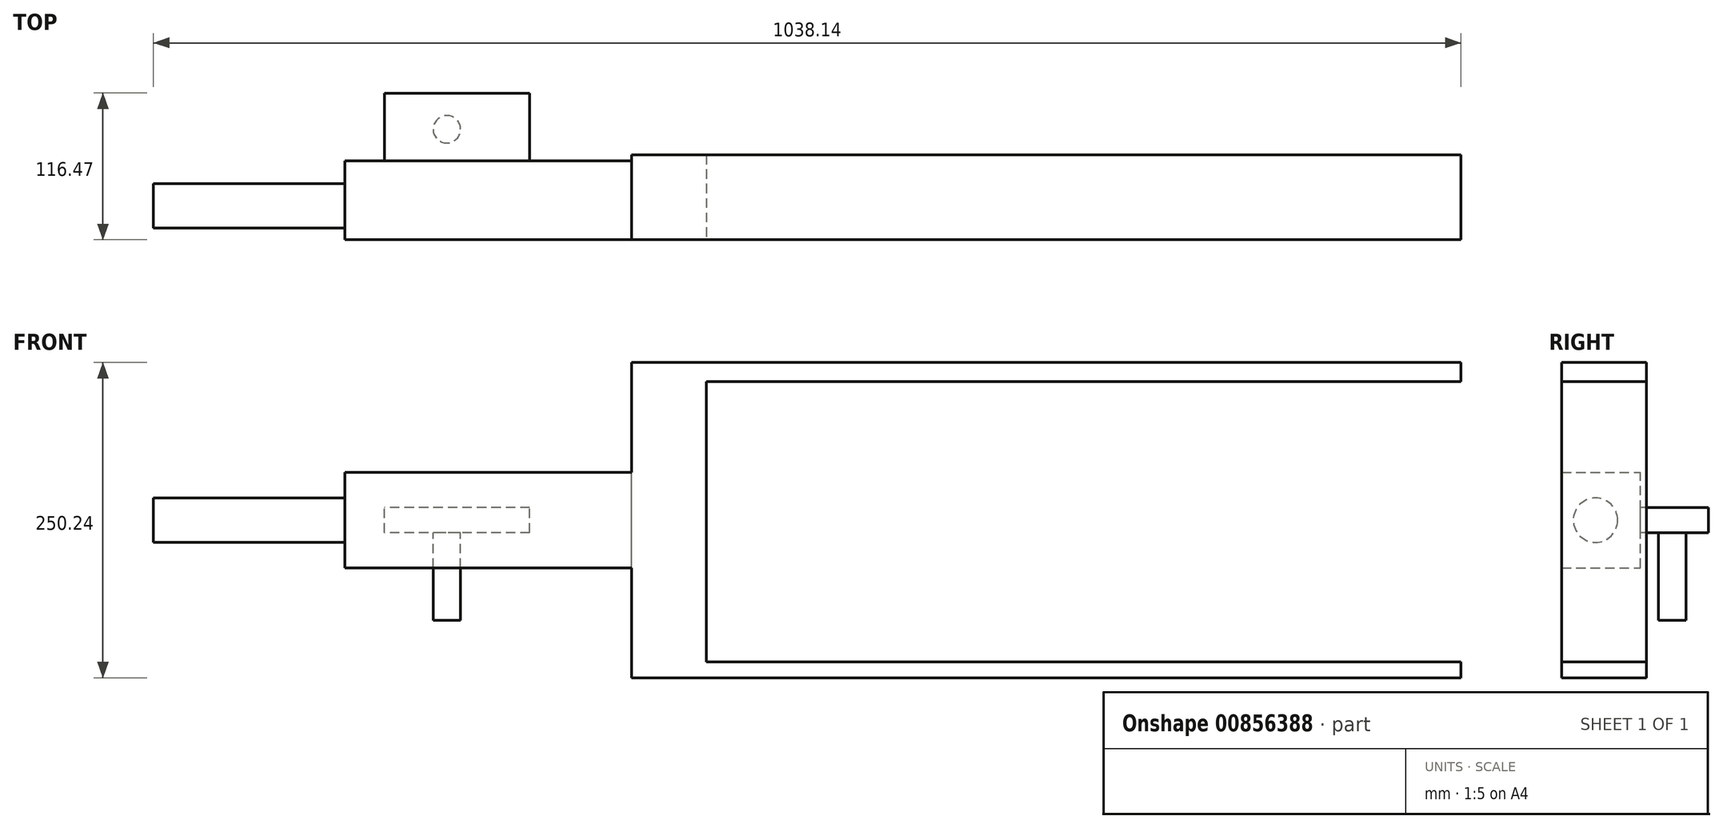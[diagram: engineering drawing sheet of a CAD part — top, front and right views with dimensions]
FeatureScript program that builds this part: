
annotation { "Feature Type Name" : "Feature", "Feature Type Description" : "" }
export const myFeature = defineFeature(function(context is Context, id is Id, definition is map)
    precondition{}
    {
        {
            var Q0;
            Q0=qCreatedBy(makeId("Front.planeOp"),FACE);
            var sketch = newSketch(context, id + "F0", { "sketchPlane" : qUnion([Q0])});
            skLineSegment(sketch, "E0.bottom", {"start": v(-29.7, -125.12) * mm, "end": v(29.7, -125.12) * mm});
            skLineSegment(sketch, "E0.top", {"start": v(-29.7, 125.12) * mm, "end": v(29.7, 125.12) * mm});
            skLineSegment(sketch, "E0.left", {"start": v(-29.7, -125.12) * mm, "end": v(-29.7, 125.12) * mm});
            skLineSegment(sketch, "E0.right", {"start": v(29.7, -125.12) * mm, "end": v(29.7, 125.12) * mm});
            skPoint(sketch, "E0.middle", {"position": v(0, 0) * mm});
            skSolve(sketch);
        }
        {
            var Q0;
            Q0 = qSketchRegion(id + "FCx6LNqj2EdK9tp_0", true);
            var Q1;
            Q1=makeQuery(id+"F0.imprint","IMPRINT",FACE,{"disambiguationData":[TD([[makeQuery(id+"F0.imprint","IMPRINT",EDGE,{"derivedFrom":sQuery(id+"F0.wireOp",EDGE,"E0.bottom")}),1.0]])]});
            extrude(context, id + "F1", {"entities" : qUnion([Q0, Q1]), "depth" : 67.44 * mm, "offsetDistance" : 25.4 * mm});
        }
        {
            var Q0;
            Q0=makeQuery(id+"F1.opExtrude","SWEPT_FACE",FACE,{"disambiguationData":[OSD([sQuery(id+"F0.wireOp",EDGE,"E0.top")])]});
            var sketch = newSketch(context, id + "F2", { "sketchPlane" : qUnion([Q0])});
            skCircle(sketch, "E1", {"center": v(0, -33.22) * mm, "radius": 17.43 * mm});
            skPoint(sketch, "E1.centerSnap0", {"position": v(0, -67.44) * mm});
            skSolve(sketch);
        }
        {
            var Q0;
            Q0=makeQuery(id+"F2.imprint","IMPRINT",FACE,{"disambiguationData":[TD([[makeQuery(id+"F2.imprint","IMPRINT",EDGE,{"derivedFrom":sQuery(id+"F2.wireOp",EDGE,"E1")}),1.0]])]});
            extrude(context, id + "F3", {"entities" : qUnion([Q0]), "operationType" : NewBodyOperationType.ADD, "oppositeDirection" : true, "depth" : 222.84 * mm, "offsetDistance" : 25.4 * mm});
        }
        {
            var Q0;
            Q0=makeQuery(id+"F1.opExtrude","SWEPT_FACE",FACE,{"disambiguationData":[OSD([sQuery(id+"F0.wireOp",EDGE,"E0.left")])]});
            var sketch = newSketch(context, id + "F4", { "sketchPlane" : qUnion([Q0])});
            skLineSegment(sketch, "E2.bottom", {"start": v(67.44, -37.79) * mm, "end": v(4.93, -37.79) * mm});
            skLineSegment(sketch, "E2.top", {"start": v(67.44, 37.79) * mm, "end": v(4.93, 37.79) * mm});
            skLineSegment(sketch, "E2.left", {"start": v(67.44, -37.79) * mm, "end": v(67.44, 37.79) * mm});
            skLineSegment(sketch, "E2.right", {"start": v(4.93, -37.79) * mm, "end": v(4.93, 37.79) * mm});
            skPoint(sketch, "E2.middle", {"position": v(36.18, 0) * mm});
            skSolve(sketch);
        }
        {
            var Q0;
            Q0=makeQuery(id+"F4.imprint","IMPRINT",FACE,{"disambiguationData":[TD([[makeQuery(id+"F4.imprint","IMPRINT",EDGE,{"derivedFrom":sQuery(id+"F4.wireOp",EDGE,"E2.bottom")}),-1.0]])]});
            extrude(context, id + "F5", {"entities" : qUnion([Q0]), "operationType" : NewBodyOperationType.ADD, "depth" : 227.65 * mm, "offsetDistance" : 25.4 * mm});
        }
        {
            var Q0;
            Q0=makeQuery(id+"F5.opExtrude","SWEPT_FACE",FACE,{"disambiguationData":[OSD([sQuery(id+"F4.wireOp",EDGE,"E2.right")])]});
            var sketch = newSketch(context, id + "F6", { "sketchPlane" : qUnion([Q0])});
            skLineSegment(sketch, "E3.bottom", {"start": v(110.41, -9.9) * mm, "end": v(225.7, -9.9) * mm});
            skLineSegment(sketch, "E3.top", {"start": v(110.41, 9.9) * mm, "end": v(225.7, 9.9) * mm});
            skLineSegment(sketch, "E3.left", {"start": v(110.41, -9.9) * mm, "end": v(110.41, 9.9) * mm});
            skLineSegment(sketch, "E3.right", {"start": v(225.7, -9.9) * mm, "end": v(225.7, 9.9) * mm});
            skPoint(sketch, "E3.middle", {"position": v(168.05, 0) * mm});
            skSolve(sketch);
        }
        {
            var Q0;
            Q0 = qSketchRegion(id + "F6", true);
            extrude(context, id + "F7", {"entities" : qUnion([Q0]), "operationType" : NewBodyOperationType.ADD, "depth" : 53.96 * mm, "offsetDistance" : 25.4 * mm});
        }
        {
            var Q0;
            Q0=makeQuery(id+"F1.opExtrude","SWEPT_FACE",FACE,{"disambiguationData":[OSD([sQuery(id+"F0.wireOp",EDGE,"E0.right")])]});
            var sketch = newSketch(context, id + "F8", { "sketchPlane" : qUnion([Q0])});
            skLineSegment(sketch, "E4.bottom", {"start": v(0, -125.12) * mm, "end": v(-67.44, -125.12) * mm});
            skLineSegment(sketch, "E4.top", {"start": v(0, -112.46) * mm, "end": v(-67.44, -112.46) * mm});
            skLineSegment(sketch, "E4.left", {"start": v(0, -125.12) * mm, "end": v(0, -112.46) * mm});
            skLineSegment(sketch, "E4.right", {"start": v(-67.44, -125.12) * mm, "end": v(-67.44, -112.46) * mm});
            skLineSegment(sketch, "E5.bottom", {"start": v(0, 125.12) * mm, "end": v(-67.44, 125.12) * mm});
            skLineSegment(sketch, "E5.top", {"start": v(0, 110.1) * mm, "end": v(-67.44, 110.1) * mm});
            skLineSegment(sketch, "E5.left", {"start": v(0, 125.12) * mm, "end": v(0, 110.1) * mm});
            skLineSegment(sketch, "E5.right", {"start": v(-67.44, 125.12) * mm, "end": v(-67.44, 110.1) * mm});
            skSolve(sketch);
        }
        {
            var Q0;
            Q0 = qSketchRegion(id + "F8", true);
            extrude(context, id + "F9", {"entities" : qUnion([Q0]), "operationType" : NewBodyOperationType.ADD, "depth" : 599.2 * mm, "offsetDistance" : 25.4 * mm});
        }
        {
            var Q0;
            Q0=makeQuery(id+"F5.opExtrude","CAP_FACE",FACE,{"disambiguationData":[OSD([sQuery(id+"F4.wireOp",EDGE,"E2.bottom"),sQuery(id+"F4.wireOp",EDGE,"E2.top"),sQuery(id+"F4.wireOp",EDGE,"E2.left"),sQuery(id+"F4.wireOp",EDGE,"E2.right")])],"isStart":false});
            var sketch = newSketch(context, id + "F10", { "sketchPlane" : qUnion([Q0])});
            skCircle(sketch, "E6", {"center": v(40.56, 0) * mm, "radius": 17.59 * mm});
            skSolve(sketch);
        }
        {
            var Q0;
            Q0=makeQuery(id+"F10.imprint","IMPRINT",FACE,{"disambiguationData":[TD([[makeQuery(id+"F10.imprint","IMPRINT",EDGE,{"derivedFrom":sQuery(id+"F10.wireOp",EDGE,"E6")}),1.0]])]});
            var Q1;
            Q1 = qSketchRegion(id + "F10", true);
            extrude(context, id + "F11", {"entities" : qUnion([Q0, Q1]), "operationType" : NewBodyOperationType.ADD, "depth" : 151.89 * mm, "offsetDistance" : 25.4 * mm});
        }
        {
            var Q0;
            Q0=makeQuery(id+"F7.opExtrude","SWEPT_FACE",FACE,{"disambiguationData":[OSD([sQuery(id+"F6.wireOp",EDGE,"E3.bottom")])]});
            var sketch = newSketch(context, id + "F12", { "sketchPlane" : qUnion([Q0])});
            skCircle(sketch, "E7", {"center": v(-176.24, -20.29) * mm, "radius": 10.9 * mm});
            skSolve(sketch);
        }
        {
            var Q0;
            Q0 = qSketchRegion(id + "F12", true);
            var Q1;
            Q1=makeQuery(id+"F12.imprint","IMPRINT",FACE,{"disambiguationData":[TD([[makeQuery(id+"F12.imprint","IMPRINT",EDGE,{"derivedFrom":sQuery(id+"F12.wireOp",EDGE,"E7")}),1.0]])]});
            extrude(context, id + "F13", {"entities" : qUnion([Q0, Q1]), "operationType" : NewBodyOperationType.ADD, "depth" : 69.47 * mm, "offsetDistance" : 25.4 * mm});
        }
    });
